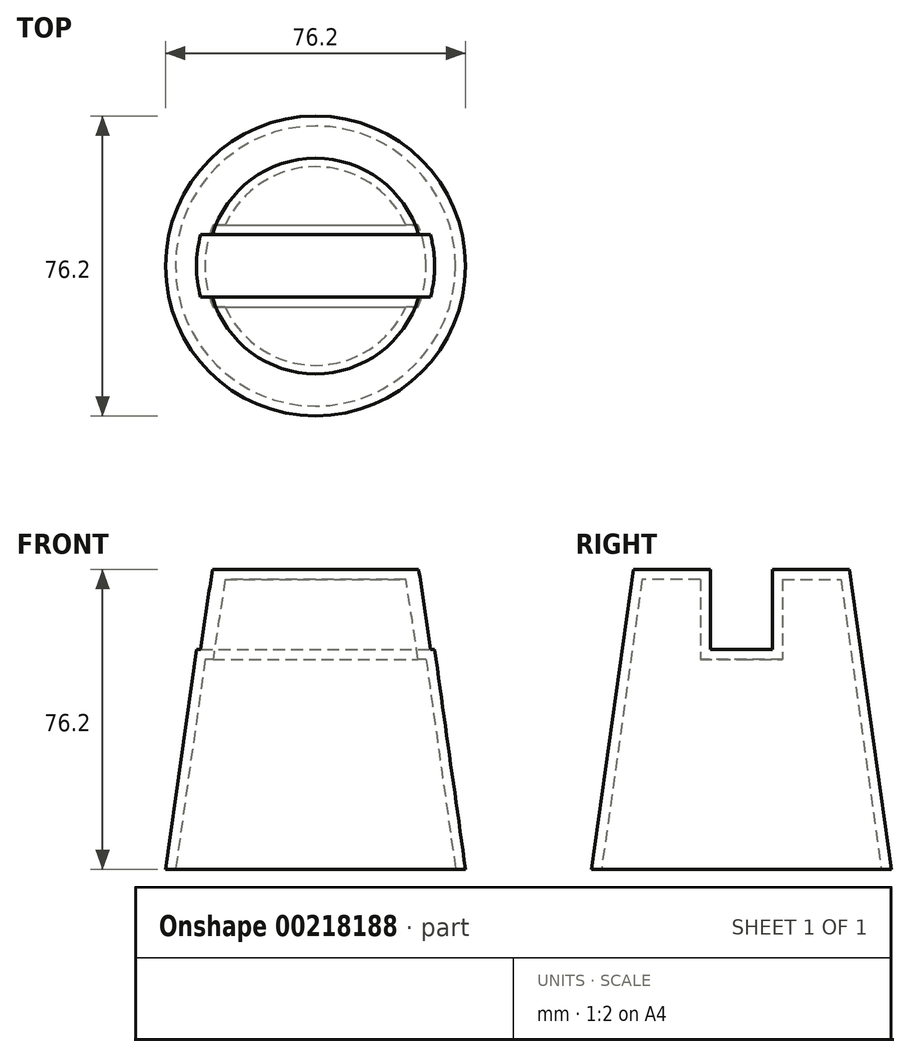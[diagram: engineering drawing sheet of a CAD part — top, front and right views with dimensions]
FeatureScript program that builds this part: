
annotation { "Feature Type Name" : "Feature", "Feature Type Description" : "" }
export const myFeature = defineFeature(function(context is Context, id is Id, definition is map)
    precondition{}
    {
        {
            var Q0;
            Q0=qCreatedBy(makeId("Top.planeOp"),FACE);
            var sketch = newSketch(context, id + "F0", { "sketchPlane" : qUnion([Q0])});
            skCircle(sketch, "E0", {"center": v(0, 0) * mm, "radius": 38.1 * mm});
            skSolve(sketch);
        }
        {
            var Q0;
            Q0=qSketchRegion(id+"F0",true);
            extrude(context, id + "F1", {"entities" : qUnion([Q0]), "depth" : 76.2 * mm, "hasDraft" : true, "draftAngle" : 8 * degree, "draftPullDirection" : true});
        }
        {
            var Q0;
            Q0=makeQuery(id+"F1.opExtrude","CAP_FACE",FACE,{"disambiguationData":[OSD([sQuery(id+"F0.wireOp",EDGE,"E0")])],"isStart":false});
            var sketch = newSketch(context, id + "F2", { "sketchPlane" : qUnion([Q0])});
            skLineSegment(sketch, "E1.bottom", {"start": v(-63.5, -7.94) * mm, "end": v(63.5, -7.94) * mm});
            skLineSegment(sketch, "E1.top", {"start": v(-63.5, 7.94) * mm, "end": v(63.5, 7.94) * mm});
            skLineSegment(sketch, "E1.left", {"start": v(-63.5, -7.94) * mm, "end": v(-63.5, 7.94) * mm});
            skLineSegment(sketch, "E1.right", {"start": v(63.5, -7.94) * mm, "end": v(63.5, 7.94) * mm});
            skPoint(sketch, "E2", {"position": v(0, 7.94) * mm});
            skPoint(sketch, "E3", {"position": v(0, -7.94) * mm});
            skPoint(sketch, "E4", {"position": v(-63.5, 0) * mm});
            skPoint(sketch, "E5", {"position": v(63.5, 0) * mm});
            skLineSegment(sketch, "E6", {"start": v(27.4, 0) * mm, "end": v(-27.4, 0) * mm, "construction": true});
            skLineSegment(sketch, "E7", {"start": v(0, 27.4) * mm, "end": v(0, -27.4) * mm, "construction": true});
            skSolve(sketch);
        }
        {
            var Q0;
            Q0=qSketchRegion(id+"F2",true);
            extrude(context, id + "F3", {"entities" : qUnion([Q0]), "operationType" : NewBodyOperationType.REMOVE, "oppositeDirection" : true, "depth" : 20.32 * mm});
        }
        {
            var Q0;
            Q0=makeQuery(id+"F1.opExtrude","CAP_FACE",FACE,{"disambiguationData":[OSD([sQuery(id+"F0.wireOp",EDGE,"E0")])],"isStart":true});
            shell(context, id + "F4", {"entities" : qUnion([Q0]), "thickness" : 2.5 * mm});
        }
    });
